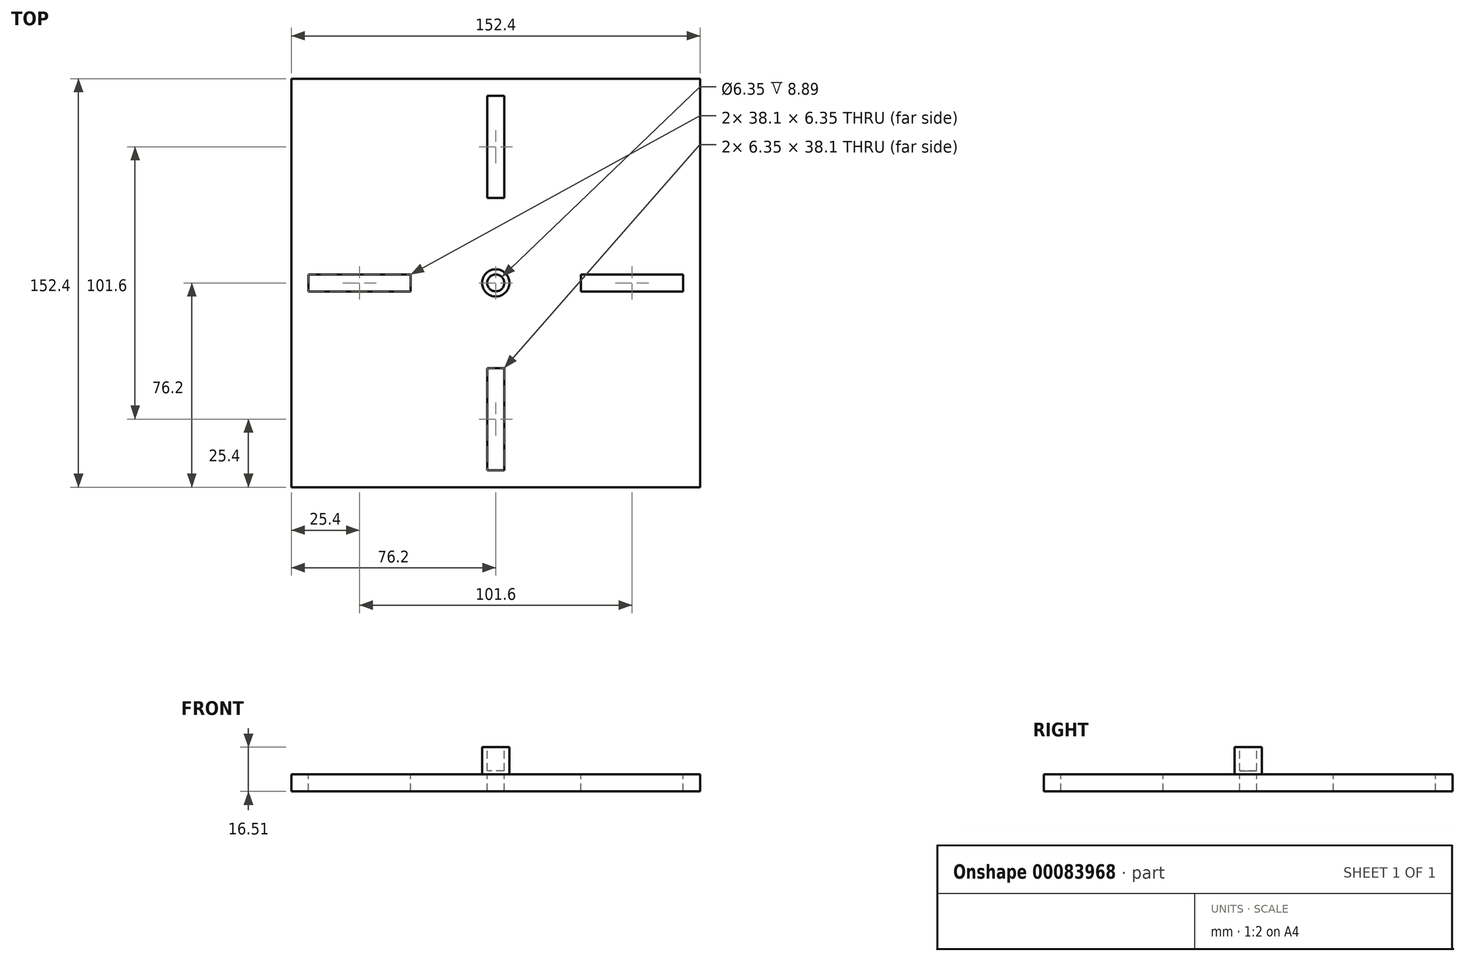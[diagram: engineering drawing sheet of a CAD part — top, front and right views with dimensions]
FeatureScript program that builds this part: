
annotation { "Feature Type Name" : "Feature", "Feature Type Description" : "" }
export const myFeature = defineFeature(function(context is Context, id is Id, definition is map)
    precondition{}
    {
        {
            var Q0;
            Q0=qCreatedBy(makeId("Top.planeOp"),FACE);
            var sketch = newSketch(context, id + "F0", { "sketchPlane" : qUnion([Q0])});
            skLineSegment(sketch, "E0.bottom", {"start": v(76.2, -76.2) * mm, "end": v(-76.2, -76.2) * mm});
            skLineSegment(sketch, "E0.top", {"start": v(76.2, 76.2) * mm, "end": v(-76.2, 76.2) * mm});
            skLineSegment(sketch, "E0.left", {"start": v(76.2, -76.2) * mm, "end": v(76.2, 76.2) * mm});
            skLineSegment(sketch, "E0.right", {"start": v(-76.2, -76.2) * mm, "end": v(-76.2, 76.2) * mm});
            skPoint(sketch, "E0.middle", {"position": v(0, 0) * mm});
            skSolve(sketch);
        }
        {
            var Q0;
            Q0 = qSketchRegion(id + "F0", true);
            extrude(context, id + "F1", {"entities" : qUnion([Q0]), "depth" : 6.35 * mm});
        }
        {
            var Q0;
            Q0=makeQuery(id+"F1.opExtrude","CAP_FACE",FACE,{"disambiguationData":[OSD([sQuery(id+"F0.wireOp",EDGE,"E0.bottom"),sQuery(id+"F0.wireOp",EDGE,"E0.top"),sQuery(id+"F0.wireOp",EDGE,"E0.left"),sQuery(id+"F0.wireOp",EDGE,"E0.right")])],"isStart":false});
            var sketch = newSketch(context, id + "F2", { "sketchPlane" : qUnion([Q0])});
            skLineSegment(sketch, "E1.bottom", {"start": v(69.85, -3.17) * mm, "end": v(31.75, -3.17) * mm});
            skLineSegment(sketch, "E1.top", {"start": v(69.85, 3.18) * mm, "end": v(31.75, 3.18) * mm});
            skLineSegment(sketch, "E1.left", {"start": v(69.85, -3.17) * mm, "end": v(69.85, 3.18) * mm});
            skLineSegment(sketch, "E1.right", {"start": v(31.75, -3.17) * mm, "end": v(31.75, 3.18) * mm});
            skSolve(sketch);
        }
        {
            var Q0;
            Q0 = qSketchRegion(id + "F2", true);
            extrude(context, id + "F3", {"entities" : qUnion([Q0]), "operationType" : NewBodyOperationType.REMOVE, "oppositeDirection" : true, "depth" : 25.4 * mm});
        }
        {
            var Q0;
            Q0=makeQuery(id+"F1.opExtrude","CAP_FACE",FACE,{"disambiguationData":[OSD([sQuery(id+"F0.wireOp",EDGE,"E0.bottom"),sQuery(id+"F0.wireOp",EDGE,"E0.top"),sQuery(id+"F0.wireOp",EDGE,"E0.left"),sQuery(id+"F0.wireOp",EDGE,"E0.right")])],"isStart":false});
            var sketch = newSketch(context, id + "F4", { "sketchPlane" : qUnion([Q0])});
            skLineSegment(sketch, "E2.bottom", {"start": v(3.18, -69.85) * mm, "end": v(-3.18, -69.85) * mm});
            skLineSegment(sketch, "E2.top", {"start": v(3.18, -31.75) * mm, "end": v(-3.17, -31.75) * mm});
            skLineSegment(sketch, "E2.left", {"start": v(3.18, -69.85) * mm, "end": v(3.18, -31.75) * mm});
            skLineSegment(sketch, "E2.right", {"start": v(-3.18, -69.85) * mm, "end": v(-3.17, -31.75) * mm});
            skSolve(sketch);
        }
        {
            var Q0;
            Q0 = qSketchRegion(id + "F4", true);
            extrude(context, id + "F5", {"entities" : qUnion([Q0]), "operationType" : NewBodyOperationType.REMOVE, "oppositeDirection" : true, "depth" : 25.4 * mm});
        }
        {
            var Q0;
            Q0=makeQuery(id+"F1.opExtrude","CAP_FACE",FACE,{"disambiguationData":[OSD([sQuery(id+"F0.wireOp",EDGE,"E0.bottom"),sQuery(id+"F0.wireOp",EDGE,"E0.top"),sQuery(id+"F0.wireOp",EDGE,"E0.left"),sQuery(id+"F0.wireOp",EDGE,"E0.right")])],"isStart":false});
            var sketch = newSketch(context, id + "F6", { "sketchPlane" : qUnion([Q0])});
            skLineSegment(sketch, "E3.bottom", {"start": v(-69.85, -3.18) * mm, "end": v(-31.75, -3.18) * mm});
            skLineSegment(sketch, "E3.top", {"start": v(-69.85, 3.17) * mm, "end": v(-31.75, 3.17) * mm});
            skLineSegment(sketch, "E3.left", {"start": v(-69.85, -3.18) * mm, "end": v(-69.85, 3.17) * mm});
            skLineSegment(sketch, "E3.right", {"start": v(-31.75, -3.18) * mm, "end": v(-31.75, 3.17) * mm});
            skSolve(sketch);
        }
        {
            var Q0;
            Q0 = qSketchRegion(id + "F6", true);
            extrude(context, id + "F7", {"entities" : qUnion([Q0]), "operationType" : NewBodyOperationType.REMOVE, "oppositeDirection" : true, "depth" : 25.4 * mm});
        }
        {
            var Q0;
            Q0=makeQuery(id+"F1.opExtrude","CAP_FACE",FACE,{"disambiguationData":[OSD([sQuery(id+"F0.wireOp",EDGE,"E0.bottom"),sQuery(id+"F0.wireOp",EDGE,"E0.top"),sQuery(id+"F0.wireOp",EDGE,"E0.left"),sQuery(id+"F0.wireOp",EDGE,"E0.right")])],"isStart":false});
            var sketch = newSketch(context, id + "F8", { "sketchPlane" : qUnion([Q0])});
            skLineSegment(sketch, "E4.bottom", {"start": v(3.18, 31.75) * mm, "end": v(-3.17, 31.75) * mm});
            skLineSegment(sketch, "E4.top", {"start": v(3.17, 69.85) * mm, "end": v(-3.18, 69.85) * mm});
            skLineSegment(sketch, "E4.left", {"start": v(3.18, 31.75) * mm, "end": v(3.17, 69.85) * mm});
            skLineSegment(sketch, "E4.right", {"start": v(-3.17, 31.75) * mm, "end": v(-3.18, 69.85) * mm});
            skSolve(sketch);
        }
        {
            var Q0;
            Q0 = qSketchRegion(id + "F8", true);
            extrude(context, id + "F9", {"entities" : qUnion([Q0]), "operationType" : NewBodyOperationType.REMOVE, "oppositeDirection" : true, "depth" : 25.4 * mm});
        }
        {
            var Q0;
            Q0=makeQuery(id+"F1.opExtrude","CAP_FACE",FACE,{"disambiguationData":[OSD([sQuery(id+"F0.wireOp",EDGE,"E0.bottom"),sQuery(id+"F0.wireOp",EDGE,"E0.top"),sQuery(id+"F0.wireOp",EDGE,"E0.left"),sQuery(id+"F0.wireOp",EDGE,"E0.right")])],"isStart":false});
            var sketch = newSketch(context, id + "F10", { "sketchPlane" : qUnion([Q0])});
            skCircle(sketch, "E5", {"center": v(0, 0) * mm, "radius": 5.08 * mm});
            skSolve(sketch);
        }
        {
            var Q0;
            Q0 = qSketchRegion(id + "F10", true);
            extrude(context, id + "F11", {"entities" : qUnion([Q0]), "operationType" : NewBodyOperationType.ADD, "depth" : 10.16 * mm});
        }
        {
            var Q0;
            Q0=makeQuery(id+"F11.opExtrude","CAP_FACE",FACE,{"disambiguationData":[OSD([sQuery(id+"F10.wireOp",EDGE,"E5")])],"isStart":false});
            var sketch = newSketch(context, id + "F12", { "sketchPlane" : qUnion([Q0])});
            skCircle(sketch, "E6", {"center": v(0, 0) * mm, "radius": 3.18 * mm});
            skSolve(sketch);
        }
        {
            var Q0;
            Q0 = qSketchRegion(id + "F12", true);
            extrude(context, id + "F13", {"entities" : qUnion([Q0]), "operationType" : NewBodyOperationType.REMOVE, "oppositeDirection" : true, "depth" : 8.9 * mm});
        }
    });
